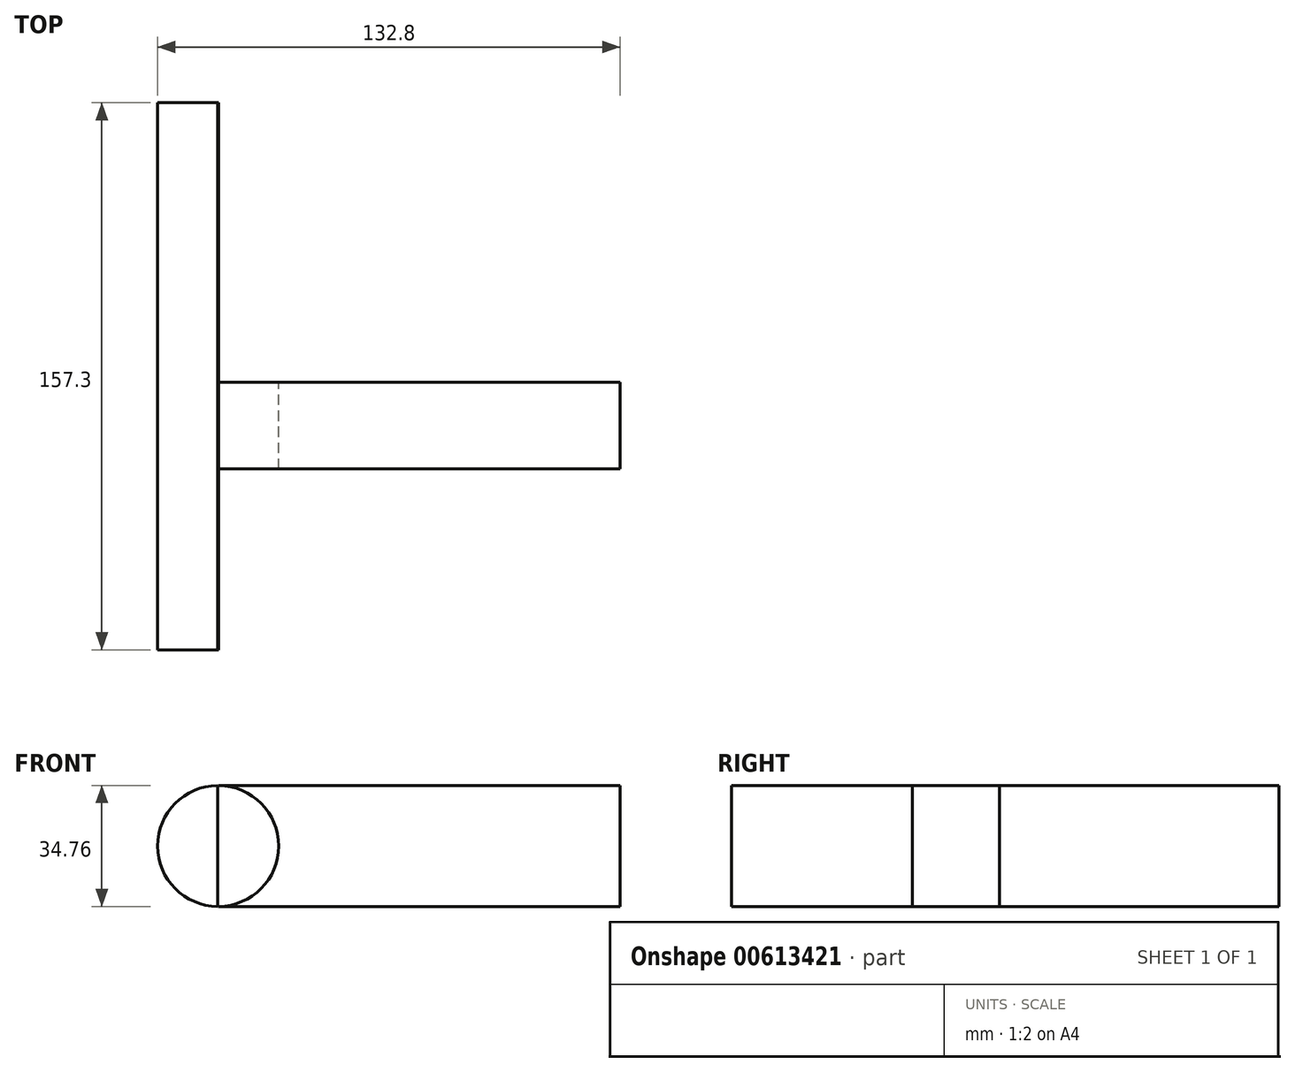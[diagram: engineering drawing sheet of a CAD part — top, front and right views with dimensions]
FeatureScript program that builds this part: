
annotation { "Feature Type Name" : "Feature", "Feature Type Description" : "" }
export const myFeature = defineFeature(function(context is Context, id is Id, definition is map)
    precondition{}
    {
        {
            var Q0;
            Q0=qCreatedBy(makeId("Front.planeOp"),FACE);
            var sketch = newSketch(context, id + "F0", { "sketchPlane" : qUnion([Q0])});
            skCircle(sketch, "E0", {"center": v(-3.74, 8.8) * mm, "radius": 17.38 * mm});
            skLineSegment(sketch, "E1.bottom", {"start": v(111.68, -8.58) * mm, "end": v(-3.92, -8.58) * mm});
            skLineSegment(sketch, "E1.top", {"start": v(111.68, 26.18) * mm, "end": v(-3.92, 26.18) * mm});
            skLineSegment(sketch, "E1.left", {"start": v(111.68, -8.58) * mm, "end": v(111.68, 26.18) * mm});
            skLineSegment(sketch, "E1.right", {"start": v(-3.92, -8.58) * mm, "end": v(-3.92, 26.18) * mm});
            skPoint(sketch, "E1.middle", {"position": v(53.88, 8.8) * mm});
            skSolve(sketch);
        }
        {
            var Q0;
            Q0=makeQuery(id+"F0.imprint","IMPRINT",FACE,{"disambiguationData":[TD([[makeQuery(id+"F0.imprint","IMPRINT",EDGE,{"derivedFrom":sQuery(id+"F0.wireOp",EDGE,"E0")}),1.0]])]});
            extrude(context, id + "F1", {"entities" : qUnion([Q0]), "depth" : 77 * mm, "offsetDistance" : 25.4 * mm, "hasSecondDirection" : true, "secondDirectionOppositeDirection" : true, "secondDirectionDepth" : 80.3 * mm});
        }
        {
            var Q0;
            {var subQ5=sQuery(id+"F0.wireOp",EDGE,"E1.left");Q0=makeQuery(id+"F0.imprint","IMPRINT",FACE,{"disambiguationData":[TD([[makeQuery(id+"F0.imprint","IMPRINT",EDGE,{"derivedFrom":subQ5}),1.0]])]});}
            extrude(context, id + "F2", {"entities" : qUnion([Q0]), "depth" : 25 * mm, "offsetDistance" : 25 * mm});
        }
    });
